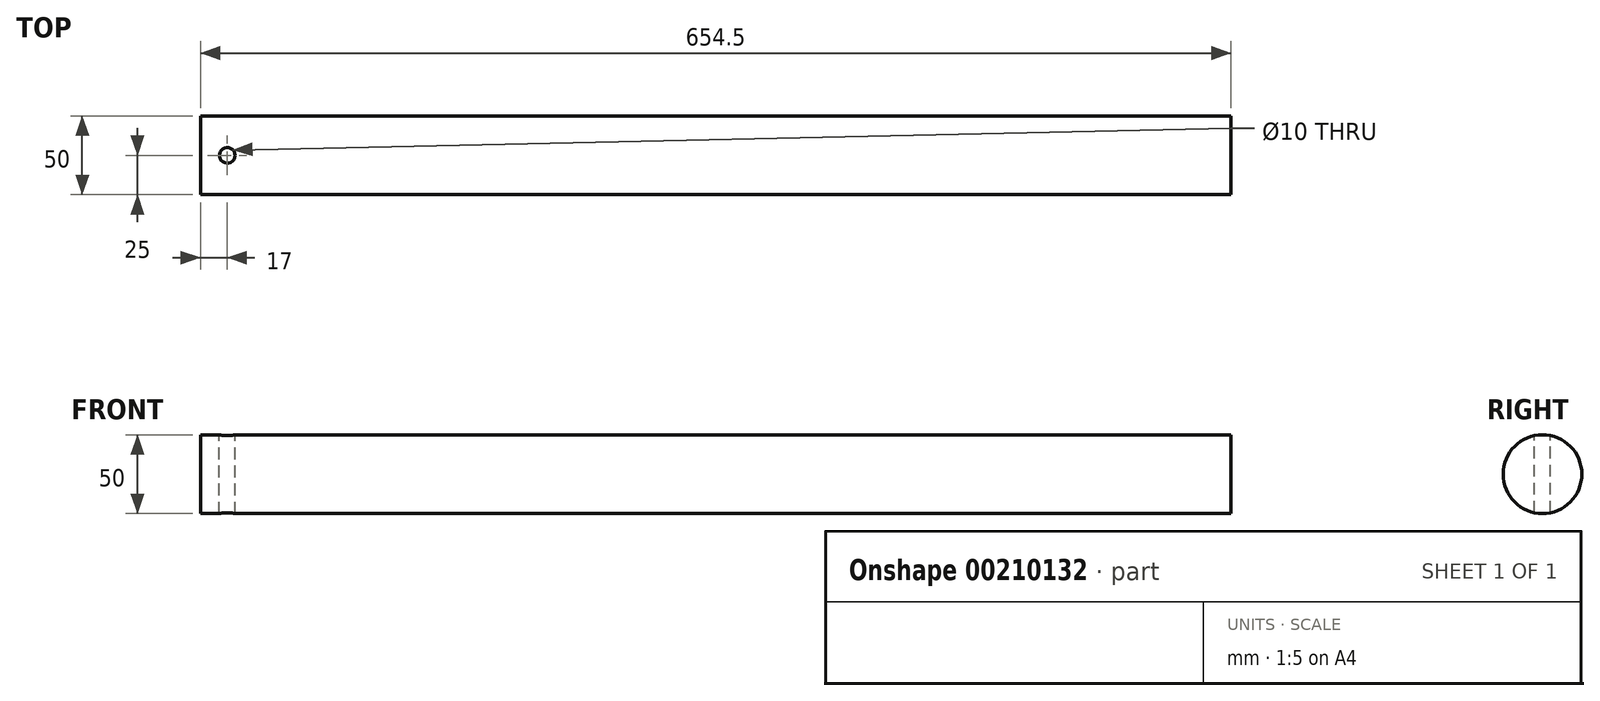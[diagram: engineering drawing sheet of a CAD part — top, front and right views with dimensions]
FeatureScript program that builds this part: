
annotation { "Feature Type Name" : "Feature", "Feature Type Description" : "" }
export const myFeature = defineFeature(function(context is Context, id is Id, definition is map)
    precondition{}
    {
        {
            var Q0;
            Q0=qCreatedBy(makeId("Right.planeOp"),FACE);
            var sketch = newSketch(context, id + "F0", { "sketchPlane" : qUnion([Q0])});
            skCircle(sketch, "E0", {"center": v(0, 0) * mm, "radius": 25 * mm});
            skSolve(sketch);
        }
        {
            var Q0;
            Q0 = qSketchRegion(id + "F0", true);
            extrude(context, id + "F1", {"entities" : qUnion([Q0]), "depth" : (1309 / 2) * mm});
        }
        {
            var Q0;
            Q0=qCreatedBy(makeId("Top.planeOp"),FACE);
            var sketch = newSketch(context, id + "F2", { "sketchPlane" : qUnion([Q0])});
            skLineSegment(sketch, "E1", {"start": v(0, 0) * mm, "end": v(17, 0) * mm});
            skCircle(sketch, "E2", {"center": v(17, 0) * mm, "radius": 5 * mm});
            skSolve(sketch);
        }
        {
            var Q0;
            Q0 = qSketchRegion(id + "F2", true);
            extrude(context, id + "F3", {"entities" : qUnion([Q0]), "operationType" : NewBodyOperationType.REMOVE, "endBound" : BoundingType.SYMMETRIC, "oppositeDirection" : true, "depth" : 50 * mm});
        }
    });
